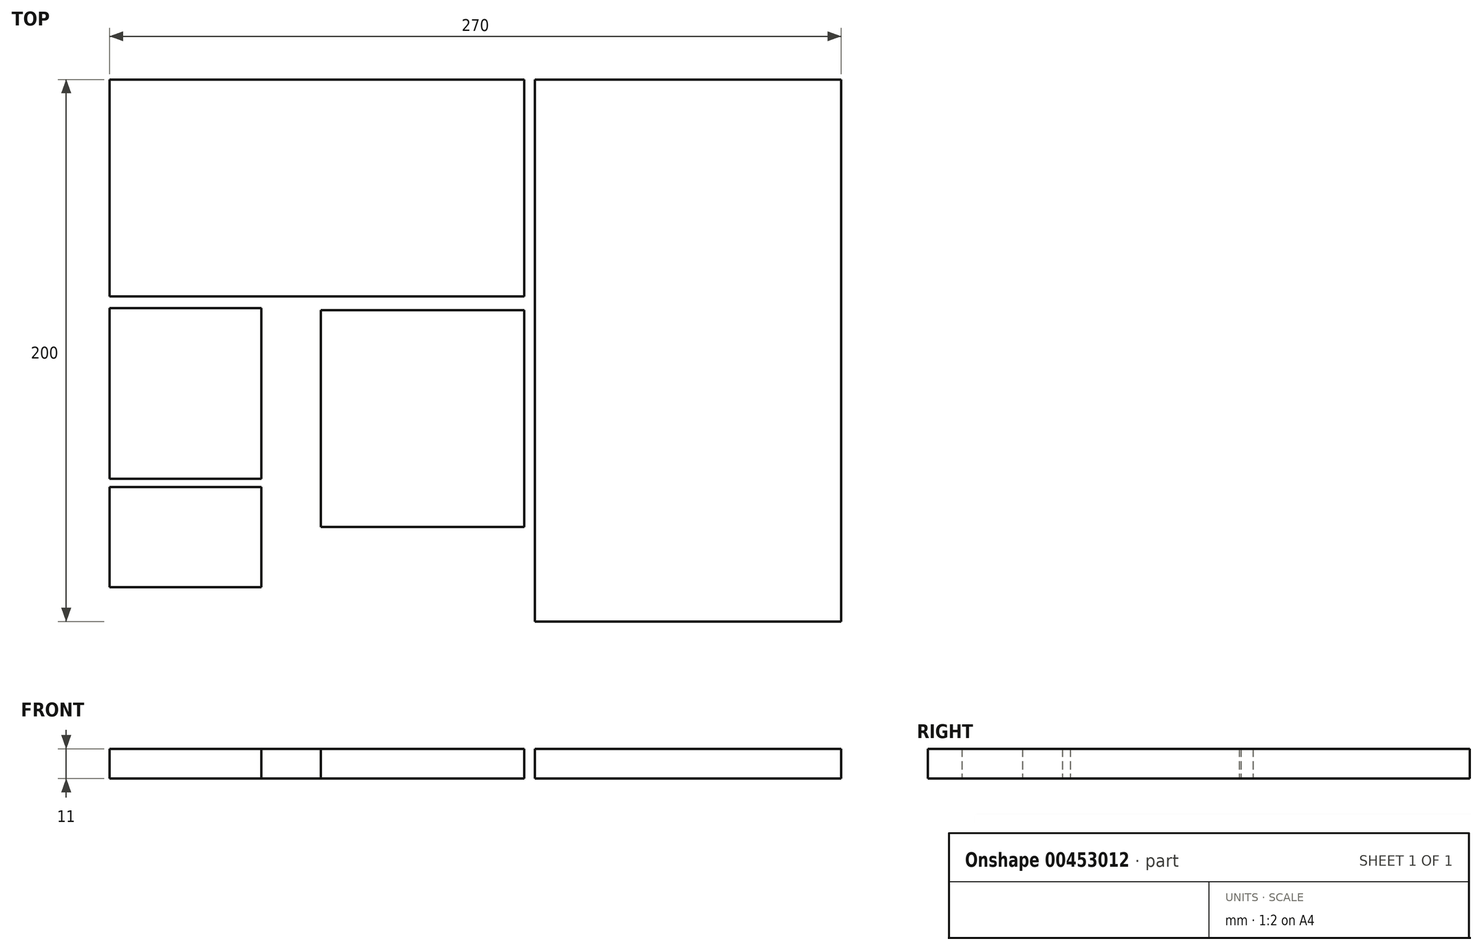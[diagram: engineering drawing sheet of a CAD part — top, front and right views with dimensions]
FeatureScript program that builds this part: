
annotation { "Feature Type Name" : "Feature", "Feature Type Description" : "" }
export const myFeature = defineFeature(function(context is Context, id is Id, definition is map)
    precondition{}
    {
        {
            var Q0;
            Q0=qCreatedBy(makeId("Top.planeOp"),FACE);
            var sketch = newSketch(context, id + "F0", { "sketchPlane" : qUnion([Q0])});
            skLineSegment(sketch, "E0.bottom", {"start": v(-135, 100) * mm, "end": v(135, 100) * mm, "construction": true});
            skLineSegment(sketch, "E0.top", {"start": v(-135, -100) * mm, "end": v(135, -100) * mm, "construction": true});
            skLineSegment(sketch, "E0.left", {"start": v(-135, 100) * mm, "end": v(-135, -100) * mm, "construction": true});
            skLineSegment(sketch, "E0.right", {"start": v(135, 100) * mm, "end": v(135, -100) * mm, "construction": true});
            skPoint(sketch, "E0.middle", {"position": v(0, 0) * mm});
            skLineSegment(sketch, "E1.bottom", {"start": v(-135, 100) * mm, "end": v(18, 100) * mm});
            skLineSegment(sketch, "E1.top", {"start": v(-135, 20) * mm, "end": v(18, 20) * mm});
            skLineSegment(sketch, "E1.left", {"start": v(-135, 100) * mm, "end": v(-135, 20) * mm});
            skLineSegment(sketch, "E1.right", {"start": v(18, 100) * mm, "end": v(18, 20) * mm});
            skLineSegment(sketch, "E2.bottom", {"start": v(-135, 15.6) * mm, "end": v(-79, 15.6) * mm});
            skLineSegment(sketch, "E2.top", {"start": v(-135, -47.4) * mm, "end": v(-79, -47.4) * mm});
            skLineSegment(sketch, "E2.left", {"start": v(-135, 15.6) * mm, "end": v(-135, -47.4) * mm});
            skLineSegment(sketch, "E2.right", {"start": v(-79, 15.6) * mm, "end": v(-79, -47.4) * mm});
            skLineSegment(sketch, "E3.bottom", {"start": v(-135, -50.38) * mm, "end": v(-79, -50.38) * mm});
            skLineSegment(sketch, "E3.top", {"start": v(-135, -87.38) * mm, "end": v(-79, -87.38) * mm});
            skLineSegment(sketch, "E3.left", {"start": v(-135, -50.38) * mm, "end": v(-135, -87.38) * mm});
            skLineSegment(sketch, "E3.right", {"start": v(-79, -50.38) * mm, "end": v(-79, -87.38) * mm});
            skLineSegment(sketch, "E4.bottom", {"start": v(18, 14.92) * mm, "end": v(-57, 14.92) * mm});
            skLineSegment(sketch, "E4.top", {"start": v(18, -65.08) * mm, "end": v(-57, -65.08) * mm});
            skLineSegment(sketch, "E4.left", {"start": v(18, 14.92) * mm, "end": v(18, -65.08) * mm});
            skLineSegment(sketch, "E4.right", {"start": v(-57, 14.92) * mm, "end": v(-57, -65.08) * mm});
            skLineSegment(sketch, "E5.bottom", {"start": v(135, 100) * mm, "end": v(22, 100) * mm});
            skLineSegment(sketch, "E5.top", {"start": v(135, -100) * mm, "end": v(22, -100) * mm});
            skLineSegment(sketch, "E5.left", {"start": v(135, 100) * mm, "end": v(135, -100) * mm});
            skLineSegment(sketch, "E5.right", {"start": v(22, 100) * mm, "end": v(22, -100) * mm});
            skSolve(sketch);
        }
        {
            var Q0;
            Q0 = qSketchRegion(id + "F0", true);
            extrude(context, id + "F1", {"entities" : qUnion([Q0]), "depth" : 11 * mm});
        }
    });
